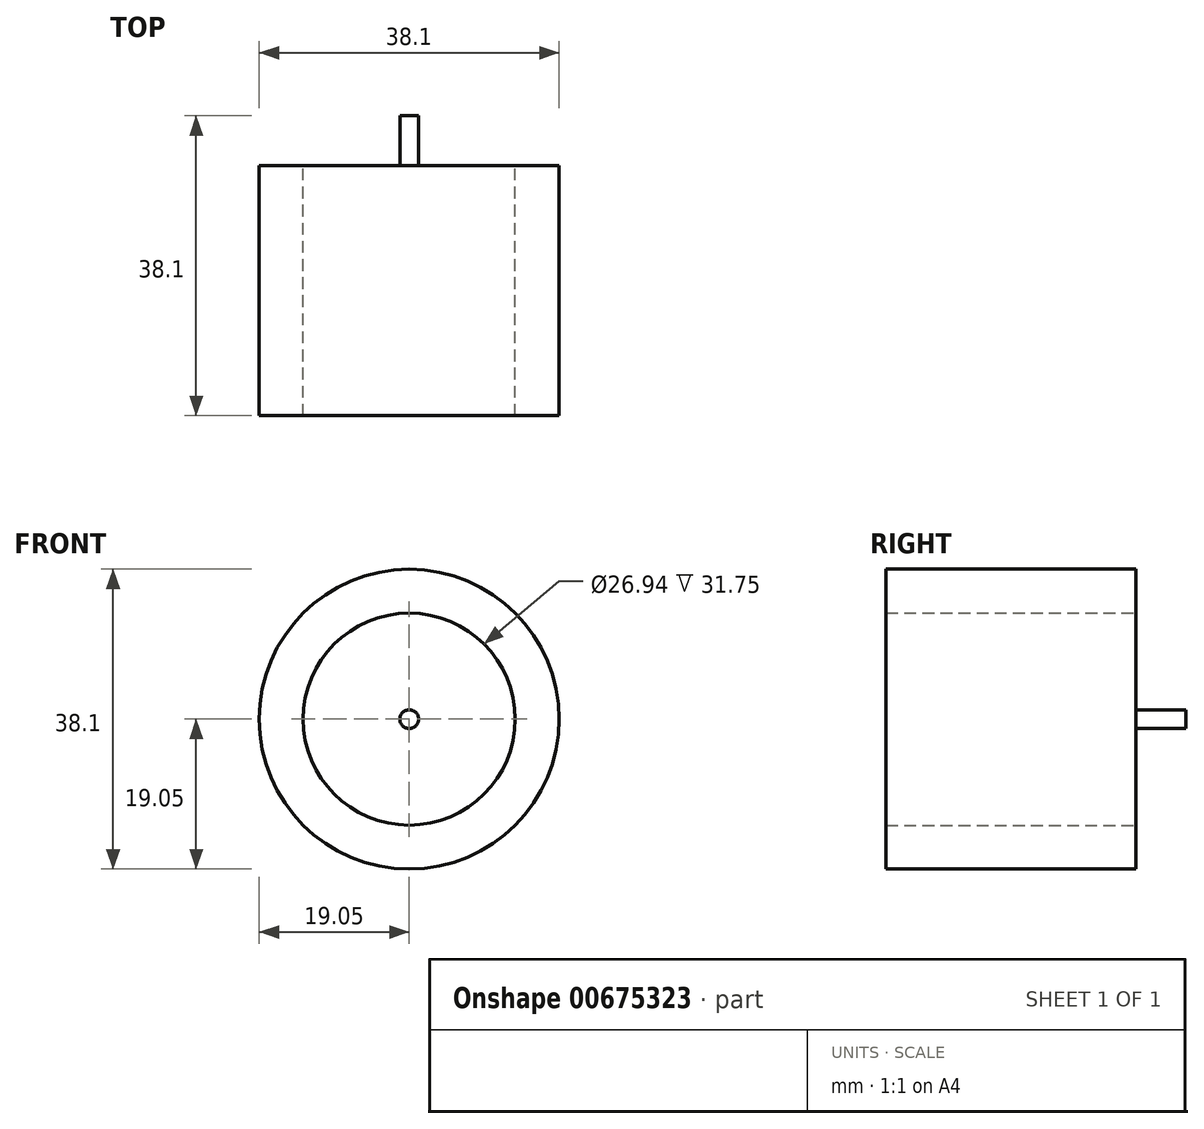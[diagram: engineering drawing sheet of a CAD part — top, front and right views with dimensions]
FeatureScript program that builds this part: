
annotation { "Feature Type Name" : "Feature", "Feature Type Description" : "" }
export const myFeature = defineFeature(function(context is Context, id is Id, definition is map)
    precondition{}
    {
        {
            var Q0;
            Q0=qCreatedBy(makeId("Front.planeOp"),FACE);
            var sketch = newSketch(context, id + "F0", { "sketchPlane" : qUnion([Q0])});
            skCircle(sketch, "E0", {"center": v(0, 0) * mm, "radius": 19.05 * mm});
            skSolve(sketch);
        }
        {
            var Q0;
            Q0 = qSketchRegion(id + "F0", true);
            extrude(context, id + "F1", {"entities" : qUnion([Q0]), "oppositeDirection" : true, "depth" : 31.75 * mm, "offsetDistance" : 25.4 * mm});
        }
        {
            var Q0;
            Q0=makeQuery(id+"F1.opExtrude","CAP_FACE",FACE,{"disambiguationData":[OSD([sQuery(id+"F0.wireOp",EDGE,"E0")])],"isStart":false});
            var sketch = newSketch(context, id + "F2", { "sketchPlane" : qUnion([Q0])});
            skCircle(sketch, "E1", {"center": v(0, 0) * mm, "radius": 1.2 * mm});
            skSolve(sketch);
        }
        {
            var Q0;
            Q0 = qSketchRegion(id + "F2", true);
            extrude(context, id + "F3", {"entities" : qUnion([Q0]), "operationType" : NewBodyOperationType.ADD, "depth" : 6.35 * mm, "offsetDistance" : 25.4 * mm});
        }
        {
            var Q0;
            Q0=makeQuery(id+"F1.opExtrude","CAP_FACE",FACE,{"disambiguationData":[OSD([sQuery(id+"F0.wireOp",EDGE,"E0")])],"isStart":false});
            var sketch = newSketch(context, id + "F4", { "sketchPlane" : qUnion([Q0])});
            skSolve(sketch);
        }
        {
            var Q0;
            Q0=makeQuery(id+"F4.imprint","IMPRINT",FACE,{"disambiguationData":[TD([[makeQuery(id+"F4.imprint","IMPRINT",EDGE,{"derivedFrom":makeQuery(id+"F1.opExtrude","CAP_EDGE",EDGE,{"disambiguationData":[OSD([sQuery(id+"F0.wireOp",EDGE,"E0")])],"isStart":false})}),-1.0]])]});
            var sketch = newSketch(context, id + "F5", { "sketchPlane" : qUnion([Q0])});
            skCircle(sketch, "E2", {"center": v(0, 0) * mm, "radius": 13.47 * mm});
            skSolve(sketch);
        }
        {
            var Q0;
            Q0 = qSketchRegion(id + "F5", true);
            extrude(context, id + "F6", {"entities" : qUnion([Q0]), "operationType" : NewBodyOperationType.REMOVE, "oppositeDirection" : true, "depth" : 38.1 * mm, "offsetDistance" : 25.4 * mm});
        }
    });
